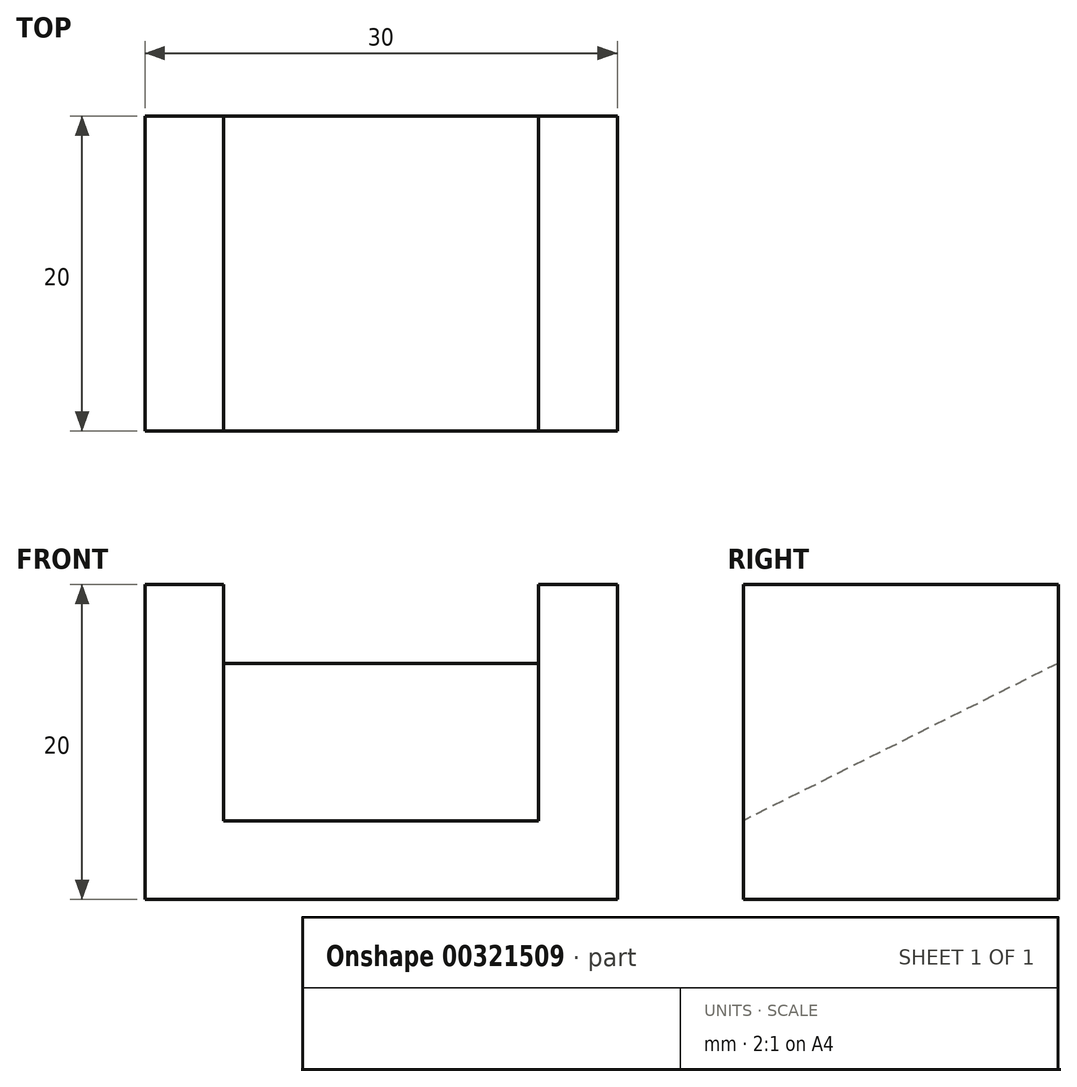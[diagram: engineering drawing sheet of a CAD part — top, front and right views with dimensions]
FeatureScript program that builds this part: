
annotation { "Feature Type Name" : "Feature", "Feature Type Description" : "" }
export const myFeature = defineFeature(function(context is Context, id is Id, definition is map)
    precondition{}
    {
        {
            var Q0;
            Q0=qCreatedBy(makeId("Front.planeOp"),FACE);
            var sketch = newSketch(context, id + "F0", { "sketchPlane" : qUnion([Q0])});
            skLineSegment(sketch, "E0", {"start": v(0, 20) * mm, "end": v(0, 0) * mm});
            skLineSegment(sketch, "E1", {"start": v(0, 0) * mm, "end": v(30, 0) * mm});
            skLineSegment(sketch, "E2", {"start": v(30, 0) * mm, "end": v(30, 20) * mm});
            skLineSegment(sketch, "E3", {"start": v(30, 20) * mm, "end": v(0, 20) * mm});
            skSolve(sketch);
        }
        {
            var Q0;
            Q0=makeQuery(id+"F0.imprint","IMPRINT",FACE,{"disambiguationData":[TD([[makeQuery(id+"F0.imprint","IMPRINT",EDGE,{"derivedFrom":sQuery(id+"F0.wireOp",EDGE,"E0")}),1.0]])]});
            extrude(context, id + "F1", {"entities" : qUnion([Q0]), "depth" : 20 * mm});
        }
        {
            var Q0;
            Q0=makeQuery(id+"F1.opExtrude","SWEPT_FACE",FACE,{"disambiguationData":[OSD([sQuery(id+"F0.wireOp",EDGE,"E2")])]});
            var sketch = newSketch(context, id + "F2", { "sketchPlane" : qUnion([Q0])});
            skLineSegment(sketch, "E4", {"start": v(-20, 5) * mm, "end": v(-20, 15) * mm});
            skLineSegment(sketch, "E5", {"start": v(-20, 15) * mm, "end": v(0, 15) * mm});
            skLineSegment(sketch, "E6", {"start": v(0, 15) * mm, "end": v(-20, 5) * mm});
            skSolve(sketch);
        }
        {
            var Q0;
            Q0=makeQuery(id+"F1.opExtrude","SWEPT_FACE",FACE,{"disambiguationData":[OSD([sQuery(id+"F0.wireOp",EDGE,"E3")])]});
            var sketch = newSketch(context, id + "F3", { "sketchPlane" : qUnion([Q0])});
            skLineSegment(sketch, "E7", {"start": v(25, -20) * mm, "end": v(25, 0) * mm});
            skLineSegment(sketch, "E8", {"start": v(5, -20) * mm, "end": v(5, 0) * mm});
            skSolve(sketch);
        }
        {
            var Q0;
            Q0 = qSketchRegion(id + "F3", true);
            var Q1;
            {var subQ0=sQuery(id+"F3.wireOp",EDGE,"E7");Q1=makeQuery(id+"F3.imprint","IMPRINT",FACE,{"disambiguationData":[TD([[makeQuery(id+"F3.imprint","IMPRINT",EDGE,{"derivedFrom":subQ0}),1.0]])]});}
            extrude(context, id + "F4", {"entities" : qUnion([Q0, Q1]), "operationType" : NewBodyOperationType.REMOVE, "oppositeDirection" : true, "depth" : 5 * mm});
        }
        {
            var Q0;
            Q0=makeQuery(id+"F2.imprint","IMPRINT",FACE,{"disambiguationData":[TD([[makeQuery(id+"F2.imprint","IMPRINT",EDGE,{"derivedFrom":sQuery(id+"F2.wireOp",EDGE,"E4")}),-1.0]])]});
            extrude(context, id + "F5", {"entities" : qUnion([Q0]), "operationType" : NewBodyOperationType.REMOVE, "oppositeDirection" : true, "depth" : 25 * mm, "hasSecondDirection" : true, "secondDirectionOppositeDirection" : true, "secondDirectionDepth" : 5 * mm});
        }
    });
